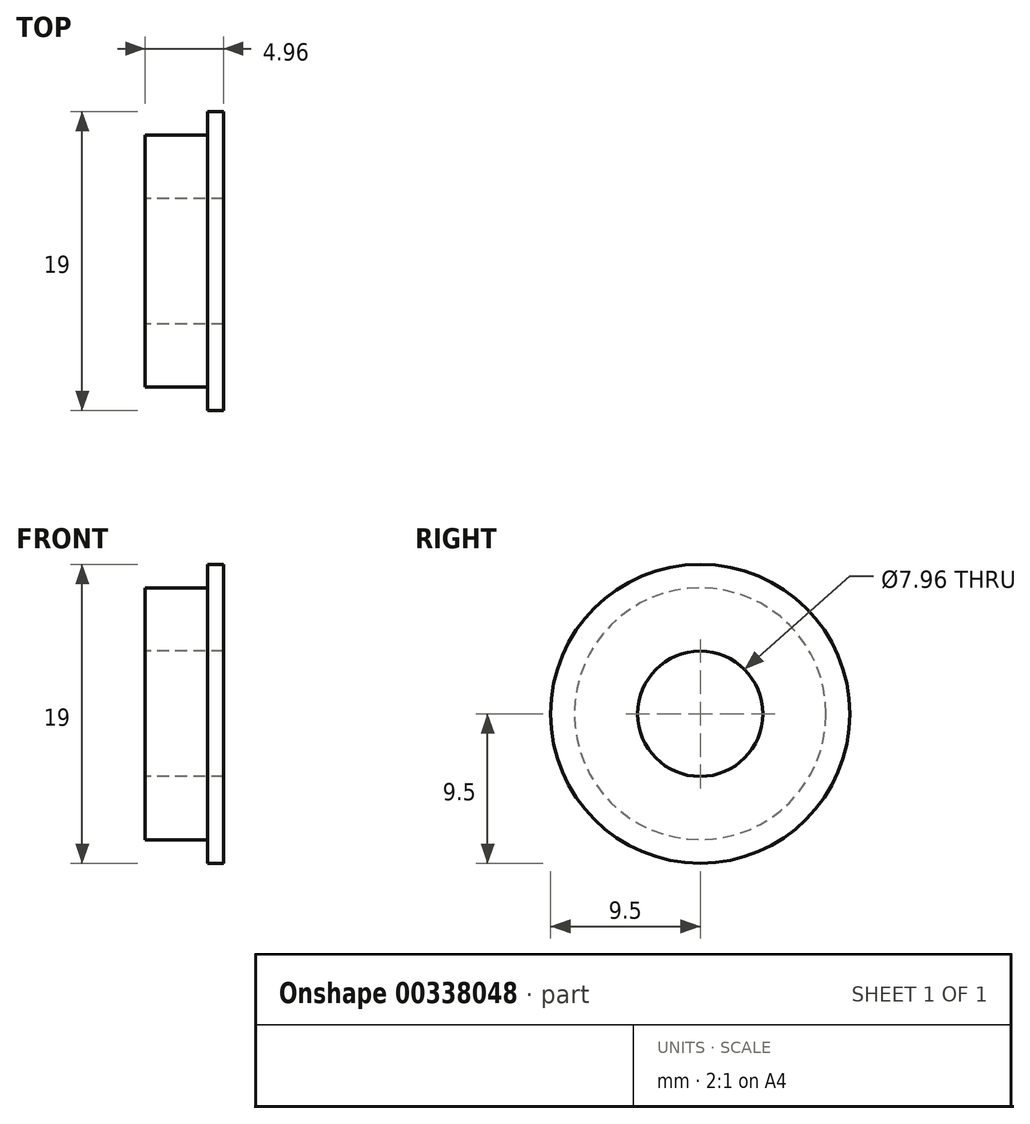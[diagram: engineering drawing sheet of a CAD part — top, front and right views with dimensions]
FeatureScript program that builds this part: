
annotation { "Feature Type Name" : "Feature", "Feature Type Description" : "" }
export const myFeature = defineFeature(function(context is Context, id is Id, definition is map)
    precondition{}
    {
        {
            var Q0;
            Q0=qCreatedBy(makeId("Right.planeOp"),FACE);
            var sketch = newSketch(context, id + "F0", { "sketchPlane" : qUnion([Q0])});
            skCircle(sketch, "E0", {"center": v(0, 0) * mm, "radius": 8 * mm});
            skCircle(sketch, "E1", {"center": v(0, 0) * mm, "radius": 3.98 * mm});
            skSolve(sketch);
        }
        {
            var Q0;
            Q0=qSketchRegion(id+"F0",true);
            extrude(context, id + "F1", {"entities" : qUnion([Q0]), "depth" : 4.96 * mm});
        }
        {
            var Q0;
            Q0=makeQuery(id+"F1.opExtrude","CAP_FACE",FACE,{"disambiguationData":[OSD([sQuery(id+"F0.wireOp",EDGE,"E0"),sQuery(id+"F0.wireOp",EDGE,"E1")])],"isStart":false});
            var sketch = newSketch(context, id + "F2", { "sketchPlane" : qUnion([Q0])});
            skCircle(sketch, "E2.0", {"center": v(0, 0) * mm, "radius": 8 * mm});
            skCircle(sketch, "E3", {"center": v(0, 0) * mm, "radius": 9.5 * mm});
            skSolve(sketch);
        }
        {
            var Q0;
            Q0=qSketchRegion(id+"F2",true);
            extrude(context, id + "F3", {"entities" : qUnion([Q0]), "operationType" : NewBodyOperationType.ADD, "oppositeDirection" : true, "depth" : 1 * mm});
        }
    });
